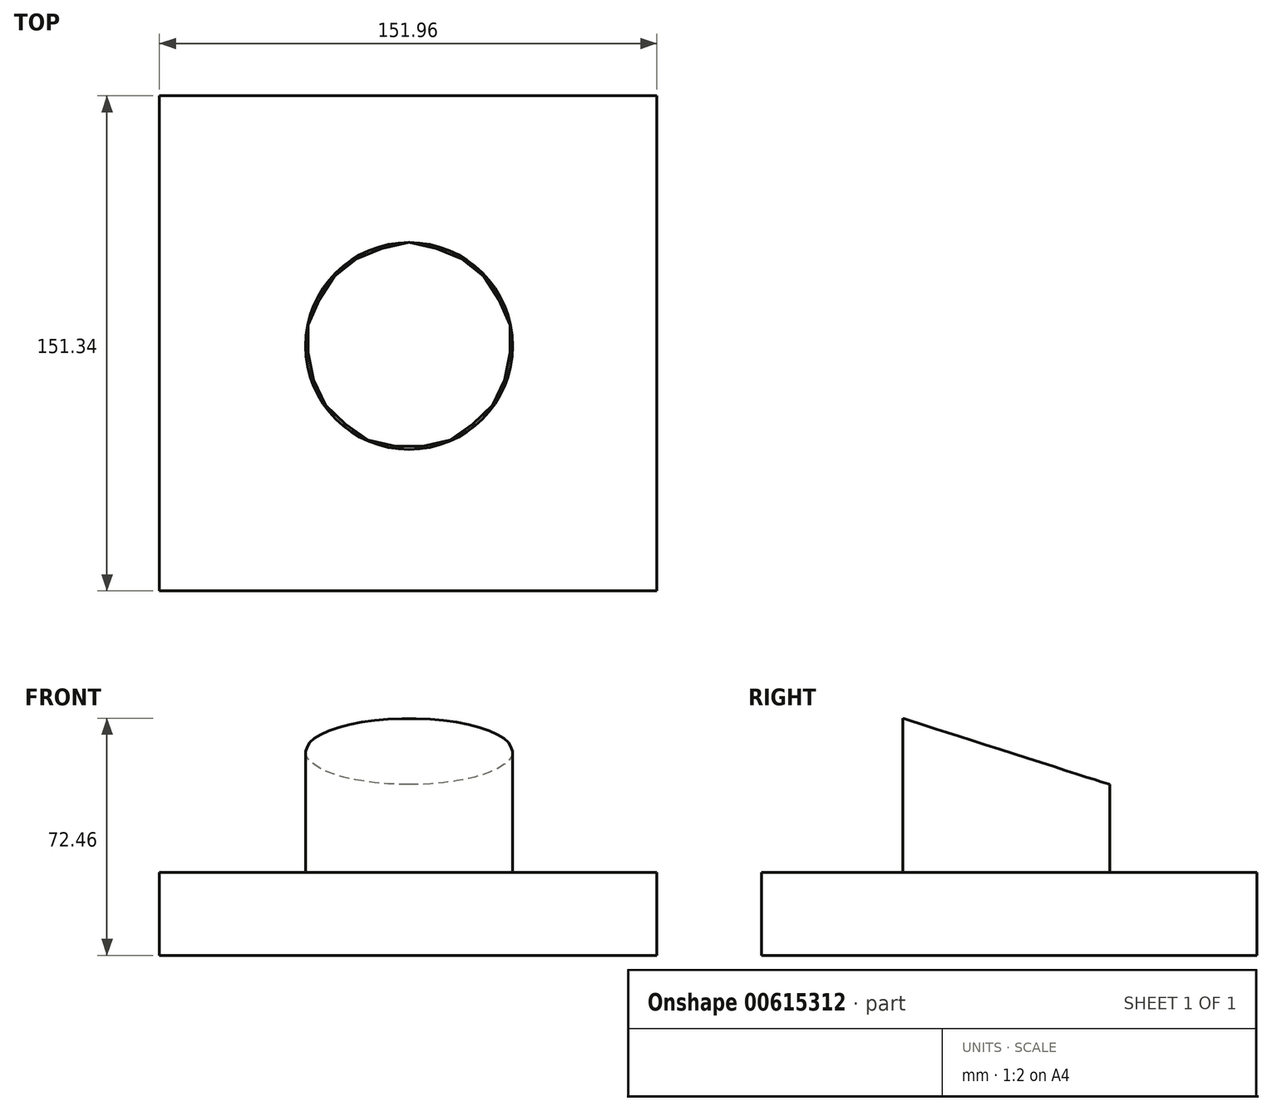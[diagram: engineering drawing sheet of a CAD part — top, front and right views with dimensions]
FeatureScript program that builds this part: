
annotation { "Feature Type Name" : "Feature", "Feature Type Description" : "" }
export const myFeature = defineFeature(function(context is Context, id is Id, definition is map)
    precondition{}
    {
        {
            var Q0;
            Q0=qCreatedBy(makeId("Top.planeOp"),FACE);
            var sketch = newSketch(context, id + "F0", { "sketchPlane" : qUnion([Q0])});
            skLineSegment(sketch, "E0.bottom", {"start": v(-76.28, -74.86) * mm, "end": v(75.68, -74.86) * mm});
            skLineSegment(sketch, "E0.top", {"start": v(-76.28, 76.48) * mm, "end": v(75.68, 76.48) * mm});
            skLineSegment(sketch, "E0.left", {"start": v(-76.28, -74.86) * mm, "end": v(-76.28, 76.48) * mm});
            skLineSegment(sketch, "E0.right", {"start": v(75.68, -74.86) * mm, "end": v(75.68, 76.48) * mm});
            skSolve(sketch);
        }
        {
            var Q0;
            Q0 = qSketchRegion(id + "F0", true);
            extrude(context, id + "F1", {"entities" : qUnion([Q0]), "depth" : 25.4 * mm, "offsetDistance" : 25.4 * mm});
        }
        {
            var Q0;
            Q0=makeQuery(id+"F1.opExtrude","CAP_FACE",FACE,{"disambiguationData":[OSD([sQuery(id+"F0.wireOp",EDGE,"E0.bottom"),sQuery(id+"F0.wireOp",EDGE,"E0.top"),sQuery(id+"F0.wireOp",EDGE,"E0.left"),sQuery(id+"F0.wireOp",EDGE,"E0.right")])],"isStart":false});
            var sketch = newSketch(context, id + "F2", { "sketchPlane" : qUnion([Q0])});
            skCircle(sketch, "E1", {"center": v(0, 0) * mm, "radius": 31.64 * mm});
            skSolve(sketch);
        }
        {
            var Q0;
            Q0 = qSketchRegion(id + "F2", true);
            extrude(context, id + "F3", {"entities" : qUnion([Q0]), "operationType" : NewBodyOperationType.ADD, "depth" : 50.8 * mm, "offsetDistance" : 25.4 * mm});
        }
        {
            var Q0;
            Q0=qCreatedBy(makeId("Right.planeOp"),FACE);
            var sketch = newSketch(context, id + "F4", { "sketchPlane" : qUnion([Q0])});
            skLineSegment(sketch, "E2", {"start": v(-43.88, 76.37) * mm, "end": v(52.56, 76.37) * mm});
            skLineSegment(sketch, "E3", {"start": v(52.56, 76.37) * mm, "end": v(52.56, 45.52) * mm});
            skLineSegment(sketch, "E4", {"start": v(52.56, 45.52) * mm, "end": v(-43.88, 76.37) * mm});
            skSolve(sketch);
        }
        {
            var Q0;
            Q0 = qSketchRegion(id + "F4", true);
            extrude(context, id + "F5", {"entities" : qUnion([Q0]), "operationType" : NewBodyOperationType.REMOVE, "endBound" : BoundingType.SYMMETRIC, "oppositeDirection" : true, "depth" : 148.84 * mm, "offsetDistance" : 25.4 * mm});
        }
    });
